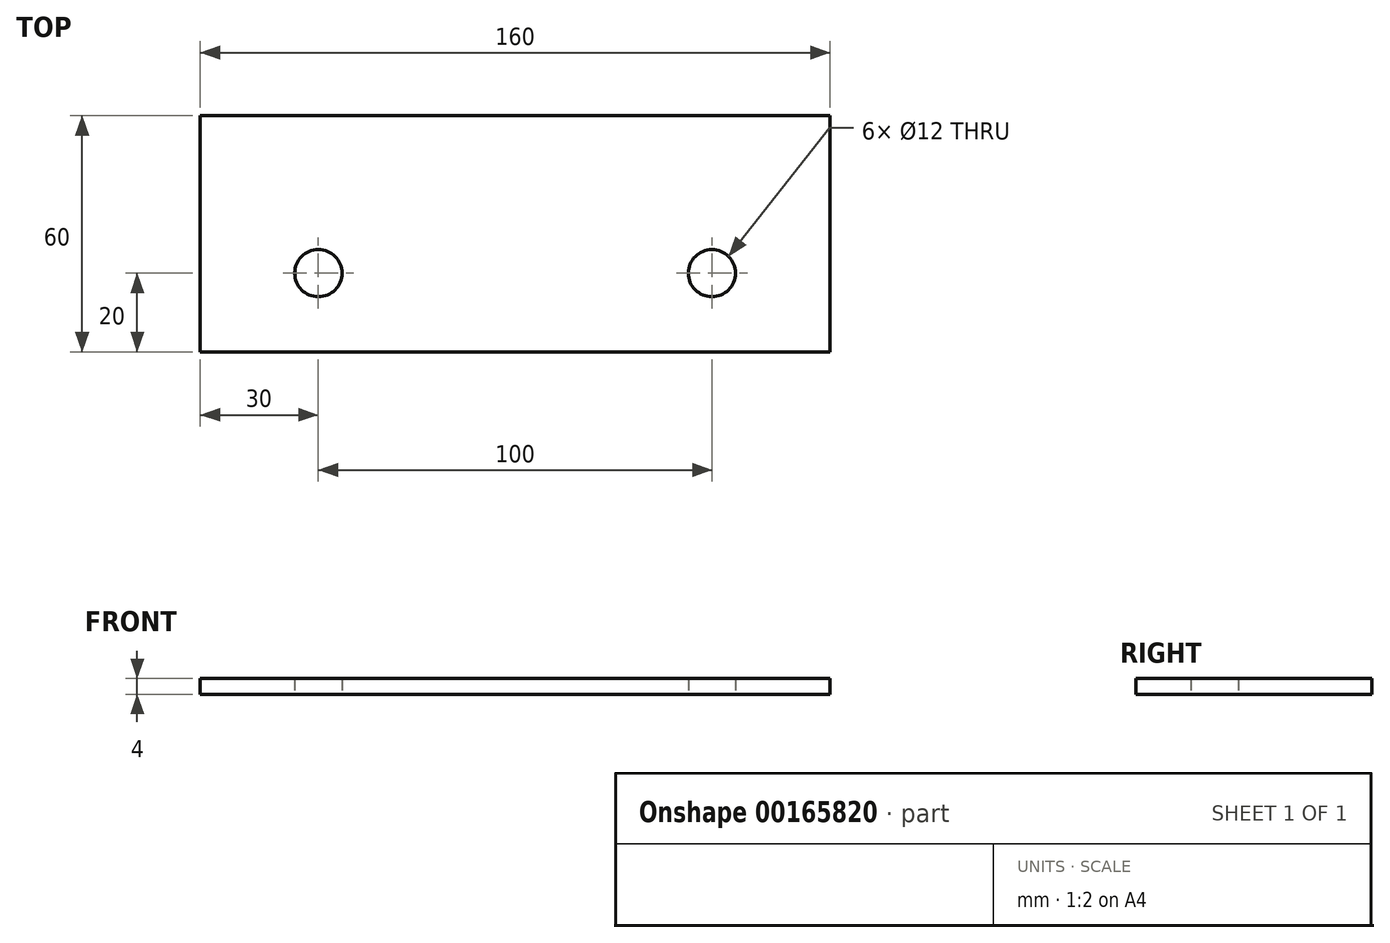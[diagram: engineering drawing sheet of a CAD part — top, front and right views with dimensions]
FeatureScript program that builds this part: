
annotation { "Feature Type Name" : "Feature", "Feature Type Description" : "" }
export const myFeature = defineFeature(function(context is Context, id is Id, definition is map)
    precondition{}
    {
        {
            var Q0;
            Q0=qCreatedBy(makeId("Top.planeOp"),FACE);
            var sketch = newSketch(context, id + "F0", { "sketchPlane" : qUnion([Q0])});
            skLineSegment(sketch, "E0.bottom", {"start": v(-80, -30) * mm, "end": v(80, -30) * mm});
            skLineSegment(sketch, "E0.top", {"start": v(-80, 30) * mm, "end": v(80, 30) * mm});
            skLineSegment(sketch, "E0.left", {"start": v(-80, -30) * mm, "end": v(-80, 30) * mm});
            skLineSegment(sketch, "E0.right", {"start": v(80, -30) * mm, "end": v(80, 30) * mm});
            skPoint(sketch, "E0.middle", {"position": v(0, 0) * mm});
            skCircle(sketch, "E1", {"center": v(-50, -10) * mm, "radius": 6 * mm});
            skCircle(sketch, "E2", {"center": v(50, -10) * mm, "radius": 6 * mm});
            skSolve(sketch);
        }
        {
            var Q0;
            Q0=makeQuery(id+"F0.imprint","IMPRINT",FACE,{"disambiguationData":[TD([[makeQuery(id+"F0.imprint","IMPRINT",EDGE,{"derivedFrom":sQuery(id+"F0.wireOp",EDGE,"E0.bottom")}),1.0]])]});
            extrude(context, id + "F1", {"entities" : qUnion([Q0]), "depth" : 4 * mm});
        }
    });
